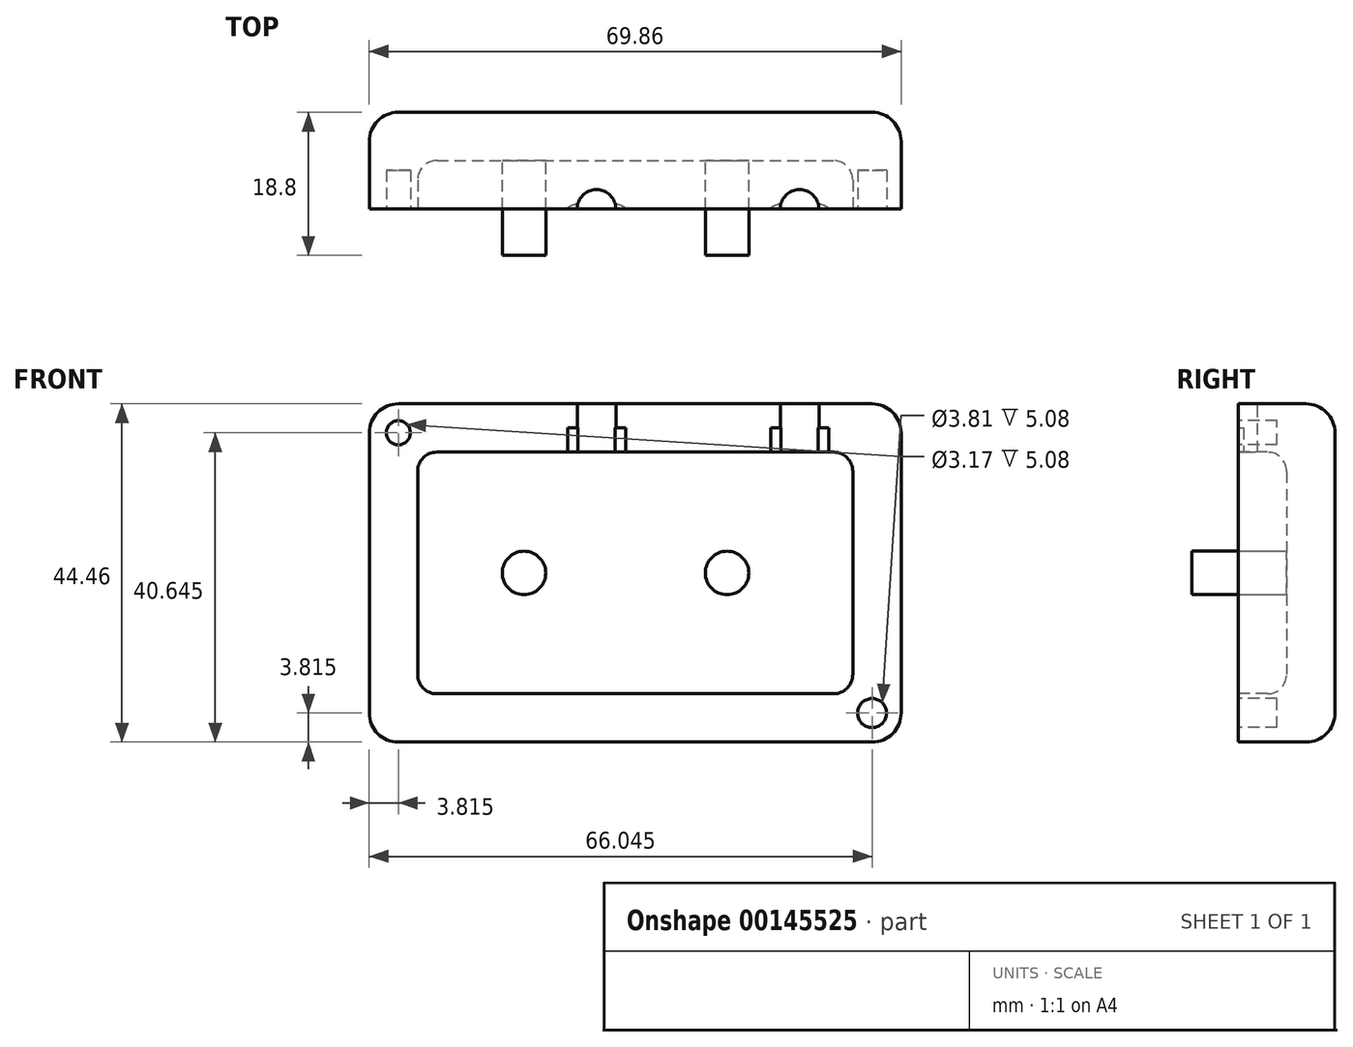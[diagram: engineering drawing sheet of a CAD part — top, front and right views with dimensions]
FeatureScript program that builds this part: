
annotation { "Feature Type Name" : "Feature", "Feature Type Description" : "" }
export const myFeature = defineFeature(function(context is Context, id is Id, definition is map)
    precondition{}
    {
        {
            var Q0;
            Q0=qCreatedBy(makeId("Front.planeOp"),FACE);
            var sketch = newSketch(context, id + "F0", { "sketchPlane" : qUnion([Q0])});
            skLineSegment(sketch, "E0.bottom", {"start": v(-34.92, 22.23) * mm, "end": v(34.93, 22.23) * mm});
            skLineSegment(sketch, "E0.top", {"start": v(-34.93, -22.22) * mm, "end": v(34.92, -22.22) * mm});
            skLineSegment(sketch, "E0.left", {"start": v(-34.93, 22.23) * mm, "end": v(-34.93, -22.22) * mm});
            skLineSegment(sketch, "E0.right", {"start": v(34.93, 22.23) * mm, "end": v(34.92, -22.22) * mm});
            skPoint(sketch, "E0.middle", {"position": v(0, 0) * mm});
            skSolve(sketch);
        }
        {
            var Q0;
            Q0 = qSketchRegion(id + "F0", true);
            extrude(context, id + "F1", {"entities" : qUnion([Q0]), "oppositeDirection" : true, "depth" : 12.7 * mm});
        }
        {
            var Q0;
            Q0=makeQuery(id+"F1.opExtrude","CAP_FACE",FACE,{"disambiguationData":[OSD([sQuery(id+"F0.wireOp",EDGE,"LqZrlxkr-7yzX-vFk0-uJjs-JSWsayYtNQzV"),sQuery(id+"F0.wireOp",EDGE,"5r0xhfTH-CSDF-mAA5-pvvG-RkQlhuwyMzcQ"),sQuery(id+"F0.wireOp",EDGE,"ef0f229b-e142-484f-bc61-ead6fe579b0b"),sQuery(id+"F0.wireOp",EDGE,"6fDFFfjc-EMaK-PeL7-7E0k-bSpFbJlcJFc0"),sQuery(id+"F0.wireOp",EDGE,"250b579a-bc1c-4dc2-aff8-3702901d077b0.MirrorCS"),sQuery(id+"F0.wireOp",EDGE,"42722c59-2561-4240-b2ed-f956cca0e4cb0.MirrorCS"),sQuery(id+"F0.wireOp",EDGE,"67368090-a0b9-42d5-ac4e-b1d2cad05f430.MirrorCS"),sQuery(id+"F0.wireOp",EDGE,"083a49a4-ea0b-41bf-8828-168f702bc1710.MirrorCS")])],"isStart":true});
            var Q1;
            Q1=makeQuery(id+"F1.opExtrude","CAP_FACE",FACE,{"disambiguationData":[OSD([sQuery(id+"F0.wireOp",EDGE,"E0.bottom"),sQuery(id+"F0.wireOp",EDGE,"E0.top"),sQuery(id+"F0.wireOp",EDGE,"E0.left"),sQuery(id+"F0.wireOp",EDGE,"E0.right")])],"isStart":true});
            shell(context, id + "F2", {"entities" : qUnion([Q0, Q1]), "thickness" : 6.35 * mm});
        }
        {
            var Q0;
            Q0=makeQuery(id+"F1.opExtrude","CAP_FACE",FACE,{"disambiguationData":[OSD([sQuery(id+"F0.wireOp",EDGE,"LqZrlxkr-7yzX-vFk0-uJjs-JSWsayYtNQzV"),sQuery(id+"F0.wireOp",EDGE,"5r0xhfTH-CSDF-mAA5-pvvG-RkQlhuwyMzcQ"),sQuery(id+"F0.wireOp",EDGE,"ef0f229b-e142-484f-bc61-ead6fe579b0b"),sQuery(id+"F0.wireOp",EDGE,"6fDFFfjc-EMaK-PeL7-7E0k-bSpFbJlcJFc0"),sQuery(id+"F0.wireOp",EDGE,"250b579a-bc1c-4dc2-aff8-3702901d077b0.MirrorCS"),sQuery(id+"F0.wireOp",EDGE,"42722c59-2561-4240-b2ed-f956cca0e4cb0.MirrorCS"),sQuery(id+"F0.wireOp",EDGE,"67368090-a0b9-42d5-ac4e-b1d2cad05f430.MirrorCS"),sQuery(id+"F0.wireOp",EDGE,"083a49a4-ea0b-41bf-8828-168f702bc1710.MirrorCS")])],"isStart":false});
            var Q1;
            Q1=makeQuery(id+"F1.opExtrude","SWEPT_EDGE",EDGE,{"disambiguationData":[OSD([sQuery(id+"F0.wireOp",EDGE,"LqZrlxkr-7yzX-vFk0-uJjs-JSWsayYtNQzV"),sQuery(id+"F0.wireOp",EDGE,"5r0xhfTH-CSDF-mAA5-pvvG-RkQlhuwyMzcQ")])]});
            var Q2;
            Q2=makeQuery(id+"F1.opExtrude","SWEPT_EDGE",EDGE,{"disambiguationData":[OSD([sQuery(id+"F0.wireOp",EDGE,"5r0xhfTH-CSDF-mAA5-pvvG-RkQlhuwyMzcQ"),sQuery(id+"F0.wireOp",EDGE,"ef0f229b-e142-484f-bc61-ead6fe579b0b")])]});
            var Q3;
            Q3=makeQuery(id+"F1.opExtrude","SWEPT_EDGE",EDGE,{"disambiguationData":[OSD([sQuery(id+"F0.wireOp",EDGE,"ef0f229b-e142-484f-bc61-ead6fe579b0b"),sQuery(id+"F0.wireOp",EDGE,"6fDFFfjc-EMaK-PeL7-7E0k-bSpFbJlcJFc0")])]});
            var Q4;
            Q4=makeQuery(id+"F1.opExtrude","SWEPT_EDGE",EDGE,{"disambiguationData":[OSD([sQuery(id+"F0.wireOp",EDGE,"250b579a-bc1c-4dc2-aff8-3702901d077b0.MirrorCS"),sQuery(id+"F0.wireOp",EDGE,"42722c59-2561-4240-b2ed-f956cca0e4cb0.MirrorCS")])]});
            var Q5;
            Q5=makeQuery(id+"F1.opExtrude","SWEPT_EDGE",EDGE,{"disambiguationData":[OSD([sQuery(id+"F0.wireOp",EDGE,"250b579a-bc1c-4dc2-aff8-3702901d077b0.MirrorCS"),sQuery(id+"F0.wireOp",EDGE,"083a49a4-ea0b-41bf-8828-168f702bc1710.MirrorCS")])]});
            var Q6;
            Q6=makeQuery(id+"F1.opExtrude","SWEPT_EDGE",EDGE,{"disambiguationData":[OSD([sQuery(id+"F0.wireOp",EDGE,"67368090-a0b9-42d5-ac4e-b1d2cad05f430.MirrorCS"),sQuery(id+"F0.wireOp",EDGE,"083a49a4-ea0b-41bf-8828-168f702bc1710.MirrorCS")])]});
            var Q7;
            Q7=makeQuery(id+"F1.opExtrude","SWEPT_EDGE",EDGE,{"disambiguationData":[OSD([sQuery(id+"F0.wireOp",EDGE,"E0.top"),sQuery(id+"F0.wireOp",EDGE,"E0.right")])]});
            var Q8;
            Q8=makeQuery(id+"F1.opExtrude","CAP_EDGE",EDGE,{"disambiguationData":[OSD([sQuery(id+"F0.wireOp",EDGE,"E0.right")])],"isStart":false});
            var Q9;
            Q9=makeQuery(id+"F1.opExtrude","CAP_EDGE",EDGE,{"disambiguationData":[OSD([sQuery(id+"F0.wireOp",EDGE,"E0.top")])],"isStart":false});
            var Q10;
            Q10=makeQuery(id+"F1.opExtrude","CAP_EDGE",EDGE,{"disambiguationData":[OSD([sQuery(id+"F0.wireOp",EDGE,"E0.left")])],"isStart":false});
            var Q11;
            Q11=makeQuery(id+"F1.opExtrude","CAP_EDGE",EDGE,{"disambiguationData":[OSD([sQuery(id+"F0.wireOp",EDGE,"E0.bottom")])],"isStart":false});
            var Q12;
            Q12=makeQuery(id+"F1.opExtrude","SWEPT_EDGE",EDGE,{"disambiguationData":[OSD([sQuery(id+"F0.wireOp",EDGE,"E0.bottom"),sQuery(id+"F0.wireOp",EDGE,"E0.left")])]});
            var Q13;
            Q13=makeQuery(id+"F1.opExtrude","SWEPT_EDGE",EDGE,{"disambiguationData":[OSD([sQuery(id+"F0.wireOp",EDGE,"E0.bottom"),sQuery(id+"F0.wireOp",EDGE,"E0.right")])]});
            var Q14;
            Q14=makeQuery(id+"F1.opExtrude","SWEPT_EDGE",EDGE,{"disambiguationData":[OSD([sQuery(id+"F0.wireOp",EDGE,"E0.top"),sQuery(id+"F0.wireOp",EDGE,"E0.left")])]});
            fillet(context, id + "F3", {"entities" : qUnion([Q0, Q1, Q2, Q3, Q4, Q5, Q6, Q7, Q8, Q9, Q10, Q11, Q12, Q13, Q14]), "radius" : 3.8 * mm, "tangentPropagation" : true, "allowEdgeOverflow" : false});
        }
        {
            var Q0;
            Q0=makeQuery(id+"F2.opShell","OFFSET_FACE",FACE,{"disambiguationData":[OSD([sQuery(id+"F0.wireOp",EDGE,"E0.bottom"),sQuery(id+"F0.wireOp",EDGE,"E0.top"),sQuery(id+"F0.wireOp",EDGE,"E0.left"),sQuery(id+"F0.wireOp",EDGE,"E0.right")])]});
            var Q1;
            Q1=makeQuery(id+"F2.opShell","OFFSET_EDGE",EDGE,{"disambiguationData":[OSD([sQuery(id+"F0.wireOp",EDGE,"E0.top"),sQuery(id+"F0.wireOp",EDGE,"E0.left")])]});
            var Q2;
            Q2=makeQuery(id+"F2.opShell","OFFSET_EDGE",EDGE,{"disambiguationData":[OSD([sQuery(id+"F0.wireOp",EDGE,"E0.top"),sQuery(id+"F0.wireOp",EDGE,"E0.right")])]});
            var Q3;
            Q3=makeQuery(id+"F2.opShell","OFFSET_EDGE",EDGE,{"disambiguationData":[OSD([sQuery(id+"F0.wireOp",EDGE,"E0.bottom"),sQuery(id+"F0.wireOp",EDGE,"E0.right")])]});
            var Q4;
            Q4=makeQuery(id+"F2.opShell","OFFSET_EDGE",EDGE,{"disambiguationData":[OSD([sQuery(id+"F0.wireOp",EDGE,"E0.bottom"),sQuery(id+"F0.wireOp",EDGE,"E0.left")])]});
            fillet(context, id + "F4", {"entities" : qUnion([Q0, Q1, Q2, Q3, Q4]), "radius" : 2.54 * mm, "tangentPropagation" : true, "allowEdgeOverflow" : false});
        }
        {
            var Q0;
            Q0=makeQuery(id+"F1.opExtrude","CAP_FACE",FACE,{"disambiguationData":[OSD([sQuery(id+"F0.wireOp",EDGE,"E0.bottom"),sQuery(id+"F0.wireOp",EDGE,"E0.top"),sQuery(id+"F0.wireOp",EDGE,"E0.left"),sQuery(id+"F0.wireOp",EDGE,"E0.right")])],"isStart":true});
            var sketch = newSketch(context, id + "F5", { "sketchPlane" : qUnion([Q0])});
            skCircle(sketch, "E1", {"center": v(-31.11, 18.42) * mm, "radius": 1.59 * mm});
            skCircle(sketch, "E2", {"center": v(31.12, -18.41) * mm, "radius": 1.9 * mm});
            skSolve(sketch);
        }
        {
            var Q0;
            Q0 = qSketchRegion(id + "F5", true);
            extrude(context, id + "F6", {"entities" : qUnion([Q0]), "operationType" : NewBodyOperationType.REMOVE, "oppositeDirection" : true, "depth" : 5.08 * mm});
        }
        {
            var Q0;
            Q0=makeQuery(id+"F2.opShell","OFFSET_FACE",FACE,{"disambiguationData":[OSD([sQuery(id+"F0.wireOp",EDGE,"E0.bottom"),sQuery(id+"F0.wireOp",EDGE,"E0.top"),sQuery(id+"F0.wireOp",EDGE,"E0.left"),sQuery(id+"F0.wireOp",EDGE,"E0.right")])]});
            var sketch = newSketch(context, id + "F7", { "sketchPlane" : qUnion([Q0])});
            skCircle(sketch, "E3", {"center": v(-14.6, 0) * mm, "radius": 2.86 * mm});
            skCircle(sketch, "E4", {"center": v(12.07, 0) * mm, "radius": 2.86 * mm});
            skSolve(sketch);
        }
        {
            var Q0;
            Q0 = qSketchRegion(id + "F7", true);
            extrude(context, id + "F8", {"entities" : qUnion([Q0]), "operationType" : NewBodyOperationType.ADD, "depth" : 12.45 * mm});
        }
        {
            var Q0;
            Q0=makeQuery(id+"F1.opExtrude","SWEPT_FACE",FACE,{"disambiguationData":[OSD([sQuery(id+"F0.wireOp",EDGE,"E0.bottom")])]});
            var sketch = newSketch(context, id + "F9", { "sketchPlane" : qUnion([Q0])});
            skLineSegment(sketch, "E5", {"start": v(-5.08, 36.75) * mm, "end": v(-5.08, -30.14) * mm, "construction": true});
            skLineSegment(sketch, "E6", {"start": v(-43.44, 0) * mm, "end": v(60.71, 0) * mm, "construction": true});
            skCircle(sketch, "E7", {"center": v(-5.08, 0) * mm, "radius": 2.54 * mm});
            skLineSegment(sketch, "E8", {"start": v(21.6, 37.05) * mm, "end": v(21.6, -29.9) * mm, "construction": true});
            skCircle(sketch, "E9", {"center": v(21.6, 0) * mm, "radius": 2.54 * mm});
            skSolve(sketch);
        }
        {
            var Q0;
            Q0 = qSketchRegion(id + "F9", true);
            var Q1;
            Q1=makeQuery(id+"F2.opShell","OFFSET_FACE",FACE,{"disambiguationData":[OSD([sQuery(id+"F0.wireOp",EDGE,"E0.bottom")])]});
            extrude(context, id + "F10", {"entities" : qUnion([Q0]), "operationType" : NewBodyOperationType.REMOVE, "endBound" : BoundingType.UP_TO_SURFACE, "oppositeDirection" : true, "endBoundEntityFace" : qUnion([Q1]), "depth" : 25.4 * mm});
        }
        {
            var Q0;
            Q0=makeQuery(id+"F2.opShell","OFFSET_FACE",FACE,{"disambiguationData":[OSD([sQuery(id+"F0.wireOp",EDGE,"E0.bottom")])]});
            var sketch = newSketch(context, id + "F11", { "sketchPlane" : qUnion([Q0])});
            skEllipse(sketch, "E10", {"center": v(-5.08, 0) * mm, "majorRadius": 3.81 * mm, "minorRadius": 0.95 * mm, "majorAxis": v(-1, 0)});
            skEllipse(sketch, "E11", {"center": v(21.6, 0) * mm, "majorRadius": 3.81 * mm, "minorRadius": 0.95 * mm, "majorAxis": v(-1, 0)});
            skSolve(sketch);
        }
        {
            var Q0;
            Q0 = qSketchRegion(id + "F11", true);
            extrude(context, id + "F12", {"entities" : qUnion([Q0]), "operationType" : NewBodyOperationType.REMOVE, "oppositeDirection" : true, "depth" : 3.17 * mm});
        }
    });
